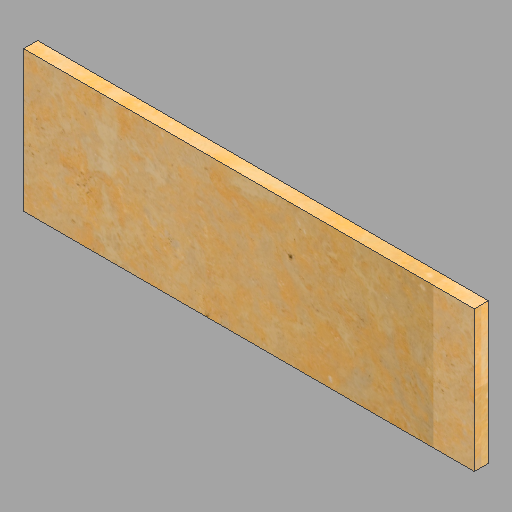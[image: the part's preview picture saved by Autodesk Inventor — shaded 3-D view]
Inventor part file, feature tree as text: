
AUTODESK INVENTOR PART (.ipt)
format: ipt  version: 2023 (Build 270158030, 158C)  size: 282,112 bytes
history: native  units: in
note: dims shown in document units (in); Inventor stores cm internally (conversion verified against a paired STEP export)
features: extrude x1, sketch x1
ambient origin geometry x8: Origin, YZ Plane, XZ Plane, XY Plane, X Axis, Y Axis, Z Axis, Center Point
bodies: Solid1 (feature_tree)
feature tree (2):
  extrude  "Extrusion1"  Depth=1.0in
  sketch  "Sketch1"  dims[d0=10.0in d1=1.0in d2=32.0in d3=0.0in]
